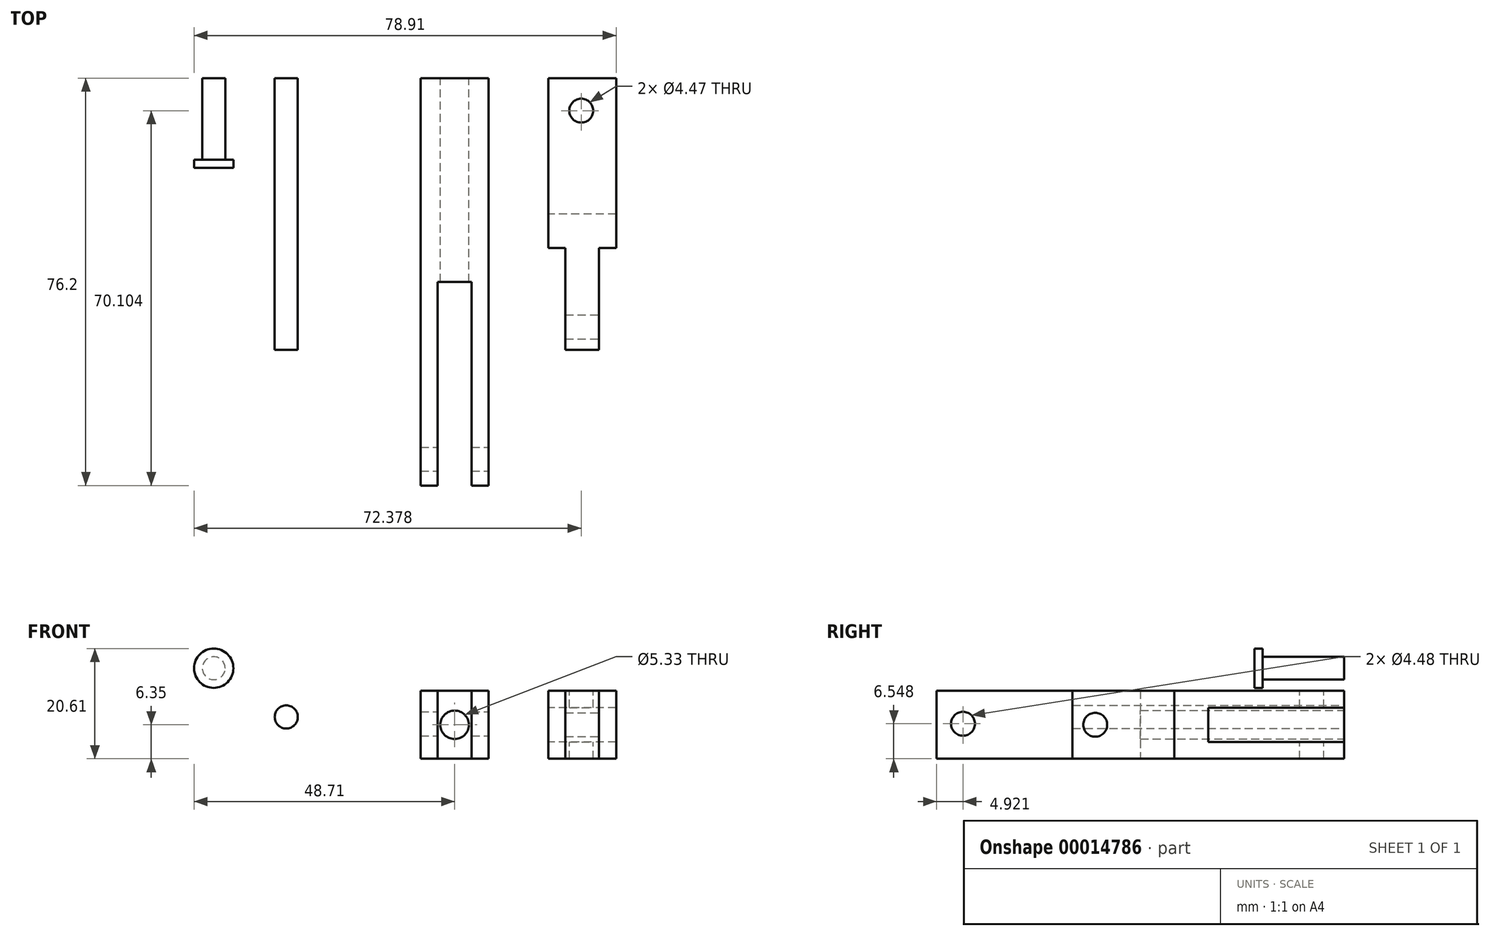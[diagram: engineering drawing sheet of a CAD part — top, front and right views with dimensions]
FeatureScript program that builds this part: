
annotation { "Feature Type Name" : "Feature", "Feature Type Description" : "" }
export const myFeature = defineFeature(function(context is Context, id is Id, definition is map)
    precondition{}
    {
        {
            var Q0;
            Q0=qCreatedBy(makeId("Front.planeOp"),FACE);
            var sketch = newSketch(context, id + "F0", { "sketchPlane" : qUnion([Q0])});
            skLineSegment(sketch, "E0.bottom", {"start": v(0, 0) * mm, "end": v(12.7, 0) * mm});
            skLineSegment(sketch, "E0.top", {"start": v(0, 12.7) * mm, "end": v(12.7, 12.7) * mm});
            skLineSegment(sketch, "E0.left", {"start": v(0, 0) * mm, "end": v(0, 12.7) * mm});
            skLineSegment(sketch, "E0.right", {"start": v(12.7, 0) * mm, "end": v(12.7, 12.7) * mm});
            skSolve(sketch);
        }
        {
            var Q0;
            Q0=makeQuery(id+"F0.imprint","IMPRINT",FACE,{"disambiguationData":[TD([[makeQuery(id+"F0.imprint","IMPRINT",EDGE,{"derivedFrom":sQuery(id+"F0.wireOp",EDGE,"E0.bottom")}),1.0]])]});
            extrude(context, id + "F1", {"entities" : qUnion([Q0]), "depth" : 76.2 * mm});
        }
        {
            var Q0;
            Q0=makeQuery(id+"F1.opExtrude","CAP_FACE",FACE,{"disambiguationData":[OSD([sQuery(id+"F0.wireOp",EDGE,"E0.bottom"),sQuery(id+"F0.wireOp",EDGE,"E0.top"),sQuery(id+"F0.wireOp",EDGE,"E0.left"),sQuery(id+"F0.wireOp",EDGE,"E0.right")])],"isStart":false});
            var sketch = newSketch(context, id + "F2", { "sketchPlane" : qUnion([Q0])});
            skLineSegment(sketch, "E1.bottom", {"start": v(3.18, 12.7) * mm, "end": v(9.53, 12.7) * mm});
            skLineSegment(sketch, "E1.top", {"start": v(3.18, 0) * mm, "end": v(9.53, 0) * mm});
            skLineSegment(sketch, "E1.left", {"start": v(3.18, 12.7) * mm, "end": v(3.18, 0) * mm});
            skLineSegment(sketch, "E1.right", {"start": v(9.53, 12.7) * mm, "end": v(9.53, 0) * mm});
            skSolve(sketch);
        }
        {
            var Q0;
            Q0 = qSketchRegion(id + "F2", true);
            extrude(context, id + "F3", {"entities" : qUnion([Q0]), "operationType" : NewBodyOperationType.REMOVE, "oppositeDirection" : true, "depth" : 38.1 * mm, "hasSecondDirection" : true, "secondDirectionOppositeDirection" : false, "secondDirectionDepth" : 25.4 * mm});
        }
        {
            var Q0;
            Q0=makeQuery(id+"F1.opExtrude","CAP_FACE",FACE,{"disambiguationData":[OSD([sQuery(id+"F0.wireOp",EDGE,"E0.bottom"),sQuery(id+"F0.wireOp",EDGE,"E0.top"),sQuery(id+"F0.wireOp",EDGE,"E0.left"),sQuery(id+"F0.wireOp",EDGE,"E0.right")])],"isStart":true});
            var sketch = newSketch(context, id + "F4", { "sketchPlane" : qUnion([Q0])});
            skCircle(sketch, "E2", {"center": v(-6.35, 6.35) * mm, "radius": 2.67 * mm});
            skSolve(sketch);
        }
        {
            var Q0;
            Q0=makeQuery(id+"F4.imprint","IMPRINT",FACE,{"disambiguationData":[TD([[makeQuery(id+"F4.imprint","IMPRINT",EDGE,{"derivedFrom":sQuery(id+"F4.wireOp",EDGE,"E2")}),1.0]])]});
            extrude(context, id + "F5", {"entities" : qUnion([Q0]), "operationType" : NewBodyOperationType.REMOVE, "oppositeDirection" : true, "depth" : 38.6 * mm});
        }
        {
            var Q0;
            Q0=makeQuery(id+"F1.opExtrude","SWEPT_FACE",FACE,{"disambiguationData":[OSD([sQuery(id+"F0.wireOp",EDGE,"E0.right")])]});
            var sketch = newSketch(context, id + "F6", { "sketchPlane" : qUnion([Q0])});
            skCircle(sketch, "E3", {"center": v(-71.28, 6.55) * mm, "radius": 2.24 * mm});
            skSolve(sketch);
        }
        {
            var Q0;
            Q0 = qSketchRegion(id + "F6", true);
            extrude(context, id + "F7", {"entities" : qUnion([Q0]), "operationType" : NewBodyOperationType.REMOVE, "oppositeDirection" : true, "depth" : 25.4 * mm});
        }
        {
            var Q0;
            Q0=qCreatedBy(makeId("Front.planeOp"),FACE);
            var sketch = newSketch(context, id + "F8", { "sketchPlane" : qUnion([Q0])});
            skLineSegment(sketch, "E4.bottom", {"start": v(23.85, 12.7) * mm, "end": v(36.55, 12.7) * mm});
            skLineSegment(sketch, "E4.top", {"start": v(23.85, 0) * mm, "end": v(36.55, 0) * mm});
            skLineSegment(sketch, "E4.left", {"start": v(23.85, 12.7) * mm, "end": v(23.85, 0) * mm});
            skLineSegment(sketch, "E4.right", {"start": v(36.55, 12.7) * mm, "end": v(36.55, 0) * mm});
            skSolve(sketch);
        }
        {
            var Q0;
            Q0 = qSketchRegion(id + "F8", true);
            extrude(context, id + "F9", {"entities" : qUnion([Q0]), "depth" : 50.8 * mm});
        }
        {
            var Q0;
            Q0=makeQuery(id+"F9.opExtrude","CAP_FACE",FACE,{"disambiguationData":[OSD([sQuery(id+"F8.wireOp",EDGE,"E4.bottom"),sQuery(id+"F8.wireOp",EDGE,"E4.top"),sQuery(id+"F8.wireOp",EDGE,"E4.left"),sQuery(id+"F8.wireOp",EDGE,"E4.right")])],"isStart":false});
            var sketch = newSketch(context, id + "F10", { "sketchPlane" : qUnion([Q0])});
            skLineSegment(sketch, "E5.bottom", {"start": v(33.35, 12.7) * mm, "end": v(36.55, 12.7) * mm});
            skLineSegment(sketch, "E5.top", {"start": v(33.35, 0) * mm, "end": v(36.55, 0) * mm});
            skLineSegment(sketch, "E5.left", {"start": v(33.35, 12.7) * mm, "end": v(33.35, 0) * mm});
            skLineSegment(sketch, "E5.right", {"start": v(36.55, 12.7) * mm, "end": v(36.55, 0) * mm});
            skLineSegment(sketch, "E6.bottom", {"start": v(23.85, 12.7) * mm, "end": v(27.05, 12.7) * mm});
            skLineSegment(sketch, "E6.top", {"start": v(23.85, 0) * mm, "end": v(27.05, 0) * mm});
            skLineSegment(sketch, "E6.left", {"start": v(23.85, 12.7) * mm, "end": v(23.85, 0) * mm});
            skLineSegment(sketch, "E6.right", {"start": v(27.05, 12.7) * mm, "end": v(27.05, 0) * mm});
            skSolve(sketch);
        }
        {
            var Q0;
            Q0 = qSketchRegion(id + "F10", true);
            extrude(context, id + "F11", {"entities" : qUnion([Q0]), "operationType" : NewBodyOperationType.REMOVE, "oppositeDirection" : true, "depth" : 19.05 * mm});
        }
        {
            var Q0;
            Q0=makeQuery(id+"F11.boolean.opBoolean","COPY",FACE,{"derivedFrom":makeQuery(id+"F11.opExtrude","SWEPT_FACE",FACE,{"disambiguationData":[OSD([sQuery(id+"F10.wireOp",EDGE,"E5.left")])]})});
            var sketch = newSketch(context, id + "F12", { "sketchPlane" : qUnion([Q0])});
            skCircle(sketch, "E7", {"center": v(-46.55, 6.36) * mm, "radius": 2.24 * mm});
            skSolve(sketch);
        }
        {
            var Q0;
            Q0 = qSketchRegion(id + "F12", true);
            extrude(context, id + "F13", {"entities" : qUnion([Q0]), "operationType" : NewBodyOperationType.REMOVE, "oppositeDirection" : true, "depth" : 15.24 * mm});
        }
        {
            var Q0;
            Q0=makeQuery(id+"F9.opExtrude","CAP_FACE",FACE,{"disambiguationData":[OSD([sQuery(id+"F8.wireOp",EDGE,"E4.bottom"),sQuery(id+"F8.wireOp",EDGE,"E4.top"),sQuery(id+"F8.wireOp",EDGE,"E4.left"),sQuery(id+"F8.wireOp",EDGE,"E4.right")])],"isStart":true});
            var sketch = newSketch(context, id + "F14", { "sketchPlane" : qUnion([Q0])});
            skLineSegment(sketch, "E8.bottom", {"start": v(-36.55, 9.55) * mm, "end": v(-23.85, 9.55) * mm});
            skLineSegment(sketch, "E8.top", {"start": v(-36.55, 3.15) * mm, "end": v(-23.85, 3.15) * mm});
            skLineSegment(sketch, "E8.left", {"start": v(-36.55, 9.55) * mm, "end": v(-36.55, 3.15) * mm});
            skLineSegment(sketch, "E8.right", {"start": v(-23.85, 9.55) * mm, "end": v(-23.85, 3.15) * mm});
            skSolve(sketch);
        }
        {
            var Q0;
            Q0 = qSketchRegion(id + "F14", true);
            extrude(context, id + "F15", {"entities" : qUnion([Q0]), "operationType" : NewBodyOperationType.REMOVE, "oppositeDirection" : true, "depth" : 25.4 * mm});
        }
        {
            var Q0;
            Q0=makeQuery(id+"F9.opExtrude","SWEPT_FACE",FACE,{"disambiguationData":[OSD([sQuery(id+"F8.wireOp",EDGE,"E4.bottom")])]});
            var sketch = newSketch(context, id + "F16", { "sketchPlane" : qUnion([Q0])});
            skCircle(sketch, "E9", {"center": v(30.02, -6.1) * mm, "radius": 2.24 * mm});
            skSolve(sketch);
        }
        {
            var Q0;
            Q0 = qSketchRegion(id + "F16", true);
            extrude(context, id + "F17", {"entities" : qUnion([Q0]), "operationType" : NewBodyOperationType.REMOVE, "oppositeDirection" : true, "depth" : 15.24 * mm});
        }
        {
            var Q0;
            Q0=qCreatedBy(makeId("Front.planeOp"),FACE);
            var sketch = newSketch(context, id + "F18", { "sketchPlane" : qUnion([Q0])});
            skCircle(sketch, "E10", {"center": v(-25.13, 7.82) * mm, "radius": 2.16 * mm});
            skSolve(sketch);
        }
        {
            var Q0;
            Q0 = qSketchRegion(id + "F18", true);
            extrude(context, id + "F19", {"entities" : qUnion([Q0]), "depth" : 50.8 * mm});
        }
        {
            var Q0;
            Q0=qCreatedBy(makeId("Front.planeOp"),FACE);
            var sketch = newSketch(context, id + "F20", { "sketchPlane" : qUnion([Q0])});
            skCircle(sketch, "E11", {"center": v(-38.69, 16.94) * mm, "radius": 2.14 * mm});
            skSolve(sketch);
        }
        {
            var Q0;
            Q0 = qSketchRegion(id + "F20", true);
            extrude(context, id + "F21", {"entities" : qUnion([Q0]), "depth" : 15.24 * mm});
        }
        {
            var Q0;
            Q0=makeQuery(id+"F21.opExtrude","CAP_FACE",FACE,{"disambiguationData":[OSD([sQuery(id+"F20.wireOp",EDGE,"E11")])],"isStart":false});
            var sketch = newSketch(context, id + "F22", { "sketchPlane" : qUnion([Q0])});
            skCircle(sketch, "E12", {"center": v(-38.69, 16.94) * mm, "radius": 3.68 * mm});
            skSolve(sketch);
        }
        {
            var Q0;
            Q0 = qSketchRegion(id + "F22", true);
            extrude(context, id + "F23", {"entities" : qUnion([Q0]), "operationType" : NewBodyOperationType.ADD, "depth" : 1.52 * mm});
        }
    });
